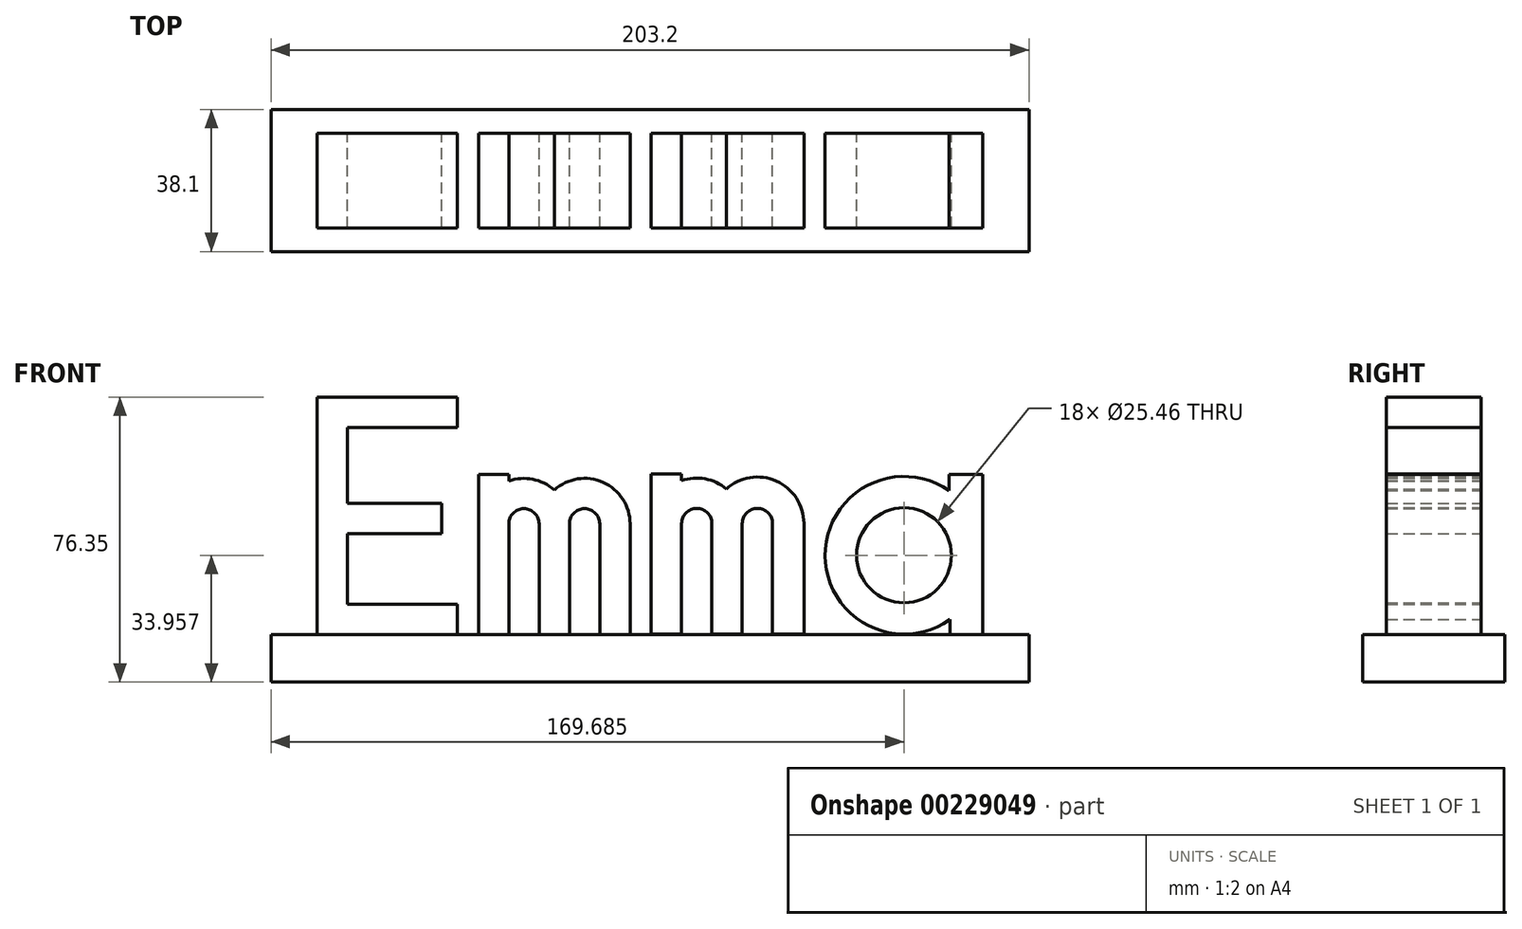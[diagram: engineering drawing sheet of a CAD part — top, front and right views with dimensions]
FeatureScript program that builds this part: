
annotation { "Feature Type Name" : "Feature", "Feature Type Description" : "" }
export const myFeature = defineFeature(function(context is Context, id is Id, definition is map)
    precondition{}
    {
        {
            var Q0;
            Q0=qCreatedBy(makeId("Front.planeOp"),FACE);
            var sketch = newSketch(context, id + "F0", { "sketchPlane" : qUnion([Q0])});
            skLineSegment(sketch, "E0.right", {"start": v(-61.44, 33.96) * mm, "end": v(-61.44, -29.7) * mm});
            skLineSegment(sketch, "E1.bottom", {"start": v(-61.44, 33.96) * mm, "end": v(-32.03, 33.96) * mm});
            skLineSegment(sketch, "E1.top", {"start": v(-61.44, 25.83) * mm, "end": v(-32.03, 25.83) * mm});
            skLineSegment(sketch, "E1.right", {"start": v(-32.03, 33.96) * mm, "end": v(-32.03, 25.83) * mm});
            skLineSegment(sketch, "E2.bottom", {"start": v(-61.44, 5.56) * mm, "end": v(-36.18, 5.56) * mm});
            skLineSegment(sketch, "E2.top", {"start": v(-61.44, -2.58) * mm, "end": v(-36.18, -2.58) * mm});
            skLineSegment(sketch, "E2.right", {"start": v(-36.18, 5.56) * mm, "end": v(-36.18, -2.58) * mm});
            skLineSegment(sketch, "E3.bottom", {"start": v(-61.44, -21.56) * mm, "end": v(-32.03, -21.56) * mm});
            skLineSegment(sketch, "E3.top", {"start": v(-63.88, -29.7) * mm, "end": v(-32.03, -29.7) * mm});
            skLineSegment(sketch, "E3.right", {"start": v(-32.03, -21.56) * mm, "end": v(-32.03, -29.7) * mm});
            skLineSegment(sketch, "E4", {"start": v(-26.33, -29.7) * mm, "end": v(-26.33, 0) * mm});
            skLineSegment(sketch, "E5.0", {"start": v(-18.2, -29.7) * mm, "end": v(-18.2, -0.01) * mm});
            skLineSegment(sketch, "E6.0", {"start": v(-10.07, -29.7) * mm, "end": v(-10.07, -0.01) * mm});
            skLineSegment(sketch, "E7.0", {"start": v(-1.94, -29.7) * mm, "end": v(-1.94, -0.01) * mm});
            skLineSegment(sketch, "E8.0", {"start": v(6.19, -29.7) * mm, "end": v(6.19, -0.01) * mm});
            skLineSegment(sketch, "E9.0", {"start": v(14.31, -29.7) * mm, "end": v(14.31, 0) * mm});
            skArc(sketch, "E10", {"start": v(-10.07, -0.01) * mm, "mid": v(-14.13, 4.05) * mm, "end": v(-18.2, -0.01) * mm});
            skArc(sketch, "E11.0", {"start": v(-1.94, 0) * mm, "mid": v(-14.14, 12.18) * mm, "end": v(-26.33, -0.01) * mm});
            skLineSegment(sketch, "E12", {"start": v(-26.33, 0) * mm, "end": v(-26.33, 13.3) * mm});
            skLineSegment(sketch, "E13", {"start": v(-18.2, -0.01) * mm, "end": v(-18.2, 13.3) * mm});
            skLineSegment(sketch, "E14", {"start": v(-18.2, 13.3) * mm, "end": v(-26.33, 13.3) * mm});
            skArc(sketch, "E15", {"start": v(6.19, -0.01) * mm, "mid": v(2.12, 4.05) * mm, "end": v(-1.94, -0.01) * mm});
            skArc(sketch, "E16.0", {"start": v(14.31, -0.01) * mm, "mid": v(2.12, 12.18) * mm, "end": v(-10.07, -0.01) * mm});
            skLineSegment(sketch, "E17", {"start": v(-26.33, -29.7) * mm, "end": v(-18.2, -29.7) * mm});
            skLineSegment(sketch, "E18", {"start": v(-10.07, -29.7) * mm, "end": v(-1.94, -29.7) * mm});
            skLineSegment(sketch, "E19", {"start": v(6.19, -29.7) * mm, "end": v(14.31, -29.7) * mm});
            skLineSegment(sketch, "E20", {"start": v(20, -29.62) * mm, "end": v(20, 0.07) * mm});
            skLineSegment(sketch, "E21.0", {"start": v(28.13, -29.62) * mm, "end": v(28.13, 0.07) * mm});
            skLineSegment(sketch, "E22.0", {"start": v(36.26, -29.62) * mm, "end": v(36.26, 0.07) * mm});
            skLineSegment(sketch, "E23.0", {"start": v(44.39, -29.62) * mm, "end": v(44.39, 0.07) * mm});
            skLineSegment(sketch, "E24.0", {"start": v(52.52, -29.62) * mm, "end": v(52.52, 0.07) * mm});
            skLineSegment(sketch, "E25.0", {"start": v(60.92, -29.62) * mm, "end": v(60.92, 0.13) * mm});
            skArc(sketch, "E26", {"start": v(36.26, 0.07) * mm, "mid": v(32.2, 4.14) * mm, "end": v(28.13, 0.07) * mm});
            skArc(sketch, "E27.0", {"start": v(44.39, 0.07) * mm, "mid": v(32.2, 12.26) * mm, "end": v(20, 0.07) * mm});
            skLineSegment(sketch, "E28", {"start": v(20, 0.07) * mm, "end": v(20, 13.37) * mm});
            skLineSegment(sketch, "E29", {"start": v(28.13, 0.07) * mm, "end": v(28.13, 13.37) * mm});
            skLineSegment(sketch, "E30", {"start": v(28.13, 13.37) * mm, "end": v(20, 13.37) * mm});
            skArc(sketch, "E31", {"start": v(52.52, 0.07) * mm, "mid": v(48.45, 4.14) * mm, "end": v(44.39, 0.07) * mm});
            skArc(sketch, "E32.0", {"start": v(60.92, 0.13) * mm, "mid": v(48.4, 12.54) * mm, "end": v(35.98, 0.02) * mm});
            skLineSegment(sketch, "E33", {"start": v(20, -29.62) * mm, "end": v(28.13, -29.62) * mm});
            skLineSegment(sketch, "E34", {"start": v(36.26, -29.62) * mm, "end": v(44.39, -29.62) * mm});
            skLineSegment(sketch, "E35", {"start": v(52.52, -29.62) * mm, "end": v(60.92, -29.62) * mm});
            skCircle(sketch, "E36", {"center": v(87.74, -8.43) * mm, "radius": 21.14 * mm});
            skPoint(sketch, "E36.first.point", {"position": v(79.73, 11.12) * mm});
            skPoint(sketch, "E36.second.point", {"position": v(80.28, -28.2) * mm});
            skPoint(sketch, "E36.third.point", {"position": v(108.88, -8.43) * mm});
            skLineSegment(sketch, "E37", {"start": v(108.88, 13.3) * mm, "end": v(108.88, -29.7) * mm});
            skLineSegment(sketch, "E38", {"start": v(100.05, -29.7) * mm, "end": v(99.8, 13.3) * mm});
            skLineSegment(sketch, "E39", {"start": v(100.05, -29.7) * mm, "end": v(108.88, -29.7) * mm});
            skLineSegment(sketch, "E40", {"start": v(99.8, 13.3) * mm, "end": v(108.88, 13.3) * mm});
            skCircle(sketch, "E41", {"center": v(87.74, -8.43) * mm, "radius": 12.73 * mm});
            skPoint(sketch, "E42.endSnap0", {"position": v(24.07, -29.62) * mm});
            skPoint(sketch, "E43.endSnap0", {"position": v(32.2, 12.26) * mm});
            skPoint(sketch, "E44.endSnap0", {"position": v(10.25, -29.7) * mm});
            skLineSegment(sketch, "E45", {"start": v(-61.44, 33.96) * mm, "end": v(-69.57, 33.96) * mm});
            skLineSegment(sketch, "E46", {"start": v(-69.57, 33.96) * mm, "end": v(-69.57, -29.7) * mm});
            skLineSegment(sketch, "E47", {"start": v(-69.57, -29.7) * mm, "end": v(-61.44, -29.7) * mm});
            skSolve(sketch);
        }
        {
            var Q0;
            {var subQ0=sQuery(id+"F0.wireOp",EDGE,"E1.bottom");Q0=makeQuery(id+"F0.imprint","IMPRINT",FACE,{"disambiguationData":[TD([[makeQuery(id+"F0.imprint","IMPRINT",EDGE,{"derivedFrom":subQ0}),-1.0]])]});}
            var Q1;
            {var subQ0=sQuery(id+"F0.wireOp",EDGE,"E2.bottom");Q1=makeQuery(id+"F0.imprint","IMPRINT",FACE,{"disambiguationData":[TD([[makeQuery(id+"F0.imprint","IMPRINT",EDGE,{"derivedFrom":subQ0}),-1.0]])]});}
            var Q2;
            {var subQ2=sQuery(id+"F0.wireOp",EDGE,"E3.bottom");Q2=makeQuery(id+"F0.imprint","IMPRINT",FACE,{"disambiguationData":[TD([[makeQuery(id+"F0.imprint","IMPRINT",EDGE,{"derivedFrom":subQ2}),-1.0]])]});}
            var Q3;
            {var subQ1=sQuery(id+"F0.wireOp",EDGE,"E0.bottom");Q3=makeQuery(id+"F0.imprint","IMPRINT",FACE,{"disambiguationData":[TD([[makeQuery(id+"F0.imprint","IMPRINT",EDGE,{"derivedFrom":subQ1}),-1.0]])]});}
            var Q4;
            {var subQ0=sQuery(id+"F0.wireOp",EDGE,"E12");Q4=makeQuery(id+"F0.imprint","IMPRINT",FACE,{"disambiguationData":[TD([[makeQuery(id+"F0.imprint","IMPRINT",EDGE,{"derivedFrom":subQ0}),-1.0]])]});}
            var Q5;
            {var subQ4=sQuery(id+"F0.wireOp",EDGE,"E4");Q5=makeQuery(id+"F0.imprint","IMPRINT",FACE,{"disambiguationData":[TD([[makeQuery(id+"F0.imprint","IMPRINT",EDGE,{"derivedFrom":subQ4}),-1.0]])]});}
            var Q6;
            {var subQ0=sQuery(id+"F0.wireOp",EDGE,"E10");Q6=makeQuery(id+"F0.imprint","IMPRINT",FACE,{"disambiguationData":[TD([[makeQuery(id+"F0.imprint","IMPRINT",EDGE,{"derivedFrom":subQ0}),-1.0]])]});}
            var Q7;
            {var subQ4=sQuery(id+"F0.wireOp",EDGE,"E6.0");Q7=makeQuery(id+"F0.imprint","IMPRINT",FACE,{"disambiguationData":[TD([[makeQuery(id+"F0.imprint","IMPRINT",EDGE,{"derivedFrom":subQ4}),-1.0]])]});}
            var Q8;
            Q8=makeQuery(id+"F0.imprint","IMPRINT",FACE,{"disambiguationData":[TD([[makeQuery(id+"F0.imprint","IMPRINT",EDGE,{"derivedFrom":sQuery(id+"F0.wireOp",EDGE,"E8.0")}),-1.0]])]});
            var Q9;
            {var subQ4=sQuery(id+"F0.wireOp",EDGE,"E20");Q9=makeQuery(id+"F0.imprint","IMPRINT",FACE,{"disambiguationData":[TD([[makeQuery(id+"F0.imprint","IMPRINT",EDGE,{"derivedFrom":subQ4}),-1.0]])]});}
            var Q10;
            {var subQ0=sQuery(id+"F0.wireOp",EDGE,"E28");Q10=makeQuery(id+"F0.imprint","IMPRINT",FACE,{"disambiguationData":[TD([[makeQuery(id+"F0.imprint","IMPRINT",EDGE,{"derivedFrom":subQ0}),-1.0]])]});}
            var Q11;
            {var subQ0=sQuery(id+"F0.wireOp",EDGE,"E26");Q11=makeQuery(id+"F0.imprint","IMPRINT",FACE,{"disambiguationData":[TD([[makeQuery(id+"F0.imprint","IMPRINT",EDGE,{"derivedFrom":subQ0}),-1.0]])]});}
            var Q12;
            {var subQ1=sQuery(id+"F0.wireOp",EDGE,"E22.0");Q12=makeQuery(id+"F0.imprint","IMPRINT",FACE,{"disambiguationData":[TD([[makeQuery(id+"F0.imprint","IMPRINT",EDGE,{"derivedFrom":subQ1}),-1.0]])]});}
            var Q13;
            Q13=makeQuery(id+"F0.imprint","IMPRINT",FACE,{"disambiguationData":[TD([[makeQuery(id+"F0.imprint","IMPRINT",EDGE,{"derivedFrom":sQuery(id+"F0.wireOp",EDGE,"E24.0")}),-1.0]])]});
            var Q14;
            {var subQ0=sQuery(id+"F0.wireOp",EDGE,"E38");var subQ1=sQuery(id+"F0.wireOp",EDGE,"E36");var subQ2=makeQuery(id+"F0.imprint","INTERSECT",VERTEX,{"disambiguationData":[OD(0.0)],"derivedFrom":[subQ1,subQ0]});Q14=makeQuery(id+"F0.imprint","IMPRINT",FACE,{"disambiguationData":[TD([[makeQuery(id+"F0.imprint","IMPRINT",EDGE,{"disambiguationData":[TD([[subQ2,-1.0]])],"derivedFrom":subQ1}),1.0]])]});}
            var Q15;
            {var subQ0=sQuery(id+"F0.wireOp",EDGE,"E38");var subQ1=sQuery(id+"F0.wireOp",EDGE,"E36");var subQ2=makeQuery(id+"F0.imprint","INTERSECT",VERTEX,{"disambiguationData":[OD(0.0)],"derivedFrom":[subQ1,subQ0]});Q15=makeQuery(id+"F0.imprint","IMPRINT",FACE,{"disambiguationData":[TD([[makeQuery(id+"F0.imprint","IMPRINT",EDGE,{"disambiguationData":[TD([[subQ2,1.0]])],"derivedFrom":subQ1}),1.0]])]});}
            var Q16;
            {var subQ5=sQuery(id+"F0.wireOp",EDGE,"E40");Q16=makeQuery(id+"F0.imprint","IMPRINT",FACE,{"disambiguationData":[TD([[makeQuery(id+"F0.imprint","IMPRINT",EDGE,{"derivedFrom":subQ5}),-1.0]])]});}
            var Q17;
            {var subQ5=sQuery(id+"F0.wireOp",EDGE,"E39");Q17=makeQuery(id+"F0.imprint","IMPRINT",FACE,{"disambiguationData":[TD([[makeQuery(id+"F0.imprint","IMPRINT",EDGE,{"derivedFrom":subQ5}),1.0]])]});}
            var Q18;
            {var subQ5=sQuery(id+"F0.wireOp",EDGE,"E45");Q18=makeQuery(id+"F0.imprint","IMPRINT",FACE,{"disambiguationData":[TD([[makeQuery(id+"F0.imprint","IMPRINT",EDGE,{"derivedFrom":subQ5}),1.0]])]});}
            extrude(context, id + "F1", {"entities" : qUnion([Q0, Q1, Q2, Q3, Q4, Q5, Q6, Q7, Q8, Q9, Q10, Q11, Q12, Q13, Q14, Q15, Q16, Q17, Q18]), "endBound" : BoundingType.SYMMETRIC, "depth" : 25.4 * mm});
        }
        {
            var Q0;
            Q0=makeQuery(id+"F1.opExtrude","SWEPT_FACE",FACE,{"disambiguationData":[OSD([sQuery(id+"F0.wireOp",EDGE,"E19")])]});
            var sketch = newSketch(context, id + "F2", { "sketchPlane" : qUnion([Q0])});
            skLineSegment(sketch, "E48.bottom", {"start": v(121.26, -19.05) * mm, "end": v(-81.94, -19.05) * mm});
            skLineSegment(sketch, "E48.top", {"start": v(121.26, 19.05) * mm, "end": v(-81.94, 19.05) * mm});
            skLineSegment(sketch, "E48.left", {"start": v(121.26, -19.05) * mm, "end": v(121.26, 19.05) * mm});
            skLineSegment(sketch, "E48.right", {"start": v(-81.94, -19.05) * mm, "end": v(-81.94, 19.05) * mm});
            skSolve(sketch);
        }
        {
            var Q0;
            Q0 = qSketchRegion(id + "F2", true);
            extrude(context, id + "F3", {"entities" : qUnion([Q0]), "depth" : 12.7 * mm});
        }
    });
